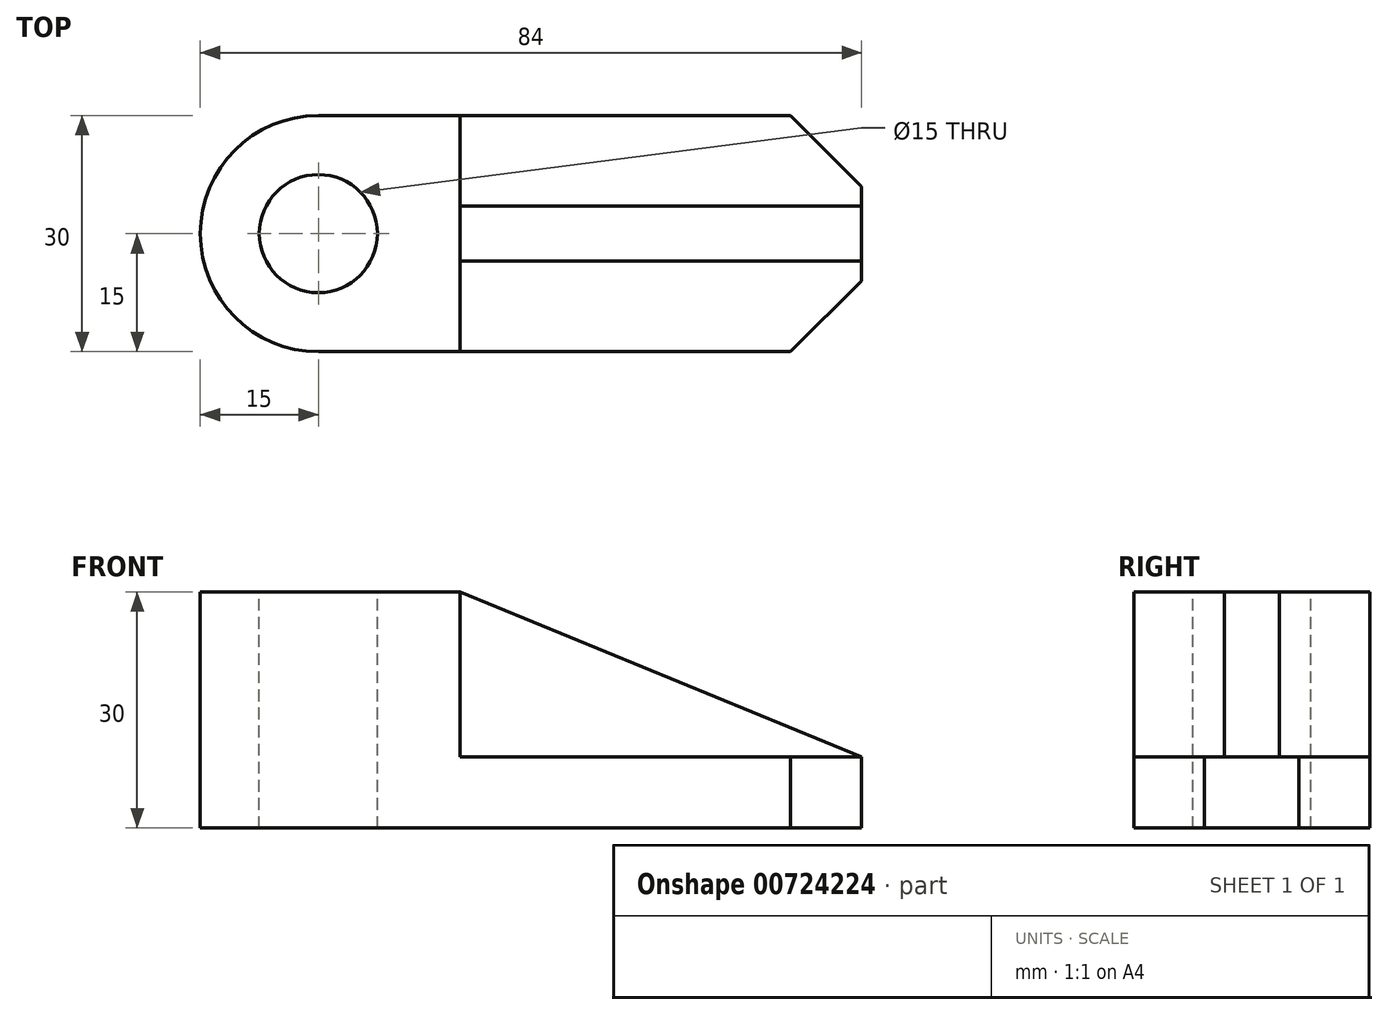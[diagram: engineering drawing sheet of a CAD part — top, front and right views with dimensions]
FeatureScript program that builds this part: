
annotation { "Feature Type Name" : "Feature", "Feature Type Description" : "" }
export const myFeature = defineFeature(function(context is Context, id is Id, definition is map)
    precondition{}
    {
        {
            var Q0;
            Q0=qCreatedBy(makeId("Top.planeOp"),FACE);
            var sketch = newSketch(context, id + "F0", { "sketchPlane" : qUnion([Q0])});
            skLineSegment(sketch, "E0", {"start": v(0, 0) * mm, "end": v(60, 0) * mm});
            skLineSegment(sketch, "E1", {"start": v(60, 0) * mm, "end": v(69, -9) * mm});
            skLineSegment(sketch, "E2", {"start": v(69, -9) * mm, "end": v(69, -21) * mm});
            skLineSegment(sketch, "E3", {"start": v(69, -21) * mm, "end": v(60, -30) * mm});
            skLineSegment(sketch, "E4", {"start": v(60, -30) * mm, "end": v(0, -30) * mm});
            skArc(sketch, "E5", {"start": v(0, 0) * mm, "mid": v(-15, -15) * mm, "end": v(0, -30) * mm});
            skSolve(sketch);
        }
        {
            var Q0;
            Q0 = qSketchRegion(id + "F0", true);
            extrude(context, id + "F1", {"entities" : qUnion([Q0]), "depth" : 9 * mm, "offsetDistance" : 25 * mm});
        }
        {
            var Q0;
            Q0=makeQuery(id+"F1.opExtrude","CAP_FACE",FACE,{"disambiguationData":[OSD([sQuery(id+"F0.wireOp",EDGE,"E0"),sQuery(id+"F0.wireOp",EDGE,"E1"),sQuery(id+"F0.wireOp",EDGE,"E2"),sQuery(id+"F0.wireOp",EDGE,"E3"),sQuery(id+"F0.wireOp",EDGE,"E4"),sQuery(id+"F0.wireOp",EDGE,"E5")])],"isStart":false});
            var sketch = newSketch(context, id + "F2", { "sketchPlane" : qUnion([Q0])});
            skLineSegment(sketch, "E6", {"start": v(18, 0) * mm, "end": v(18, -30) * mm});
            skSolve(sketch);
        }
        {
            var Q0;
            {var subQ0=sQuery(id+"F2.wireOp",EDGE,"E6");Q0=makeQuery(id+"F2.imprint","IMPRINT",FACE,{"disambiguationData":[TD([[makeQuery(id+"F2.imprint","IMPRINT",EDGE,{"derivedFrom":subQ0}),-1.0]])]});}
            extrude(context, id + "F3", {"entities" : qUnion([Q0]), "operationType" : NewBodyOperationType.ADD, "depth" : 21 * mm, "offsetDistance" : 25 * mm});
        }
        {
            var Q0;
            Q0=makeQuery(id+"F3.opExtrude","CAP_FACE",FACE,{"disambiguationData":[OSD([sQuery(id+"F0.wireOp",EDGE,"E0"),sQuery(id+"F0.wireOp",EDGE,"E4"),sQuery(id+"F0.wireOp",EDGE,"E5"),sQuery(id+"F2.wireOp",EDGE,"E6")])],"isStart":false});
            var sketch = newSketch(context, id + "F4", { "sketchPlane" : qUnion([Q0])});
            skCircle(sketch, "E7", {"center": v(0, -15) * mm, "radius": 7.5 * mm});
            skSolve(sketch);
        }
        {
            var Q0;
            Q0 = qSketchRegion(id + "F4", true);
            extrude(context, id + "F5", {"entities" : qUnion([Q0]), "operationType" : NewBodyOperationType.REMOVE, "oppositeDirection" : true, "depth" : 30 * mm, "offsetDistance" : 25 * mm});
        }
        {
            var Q0;
            Q0=makeQuery(id+"F1.opExtrude","CAP_FACE",FACE,{"disambiguationData":[OSD([sQuery(id+"F0.wireOp",EDGE,"E0"),sQuery(id+"F0.wireOp",EDGE,"E1"),sQuery(id+"F0.wireOp",EDGE,"E2"),sQuery(id+"F0.wireOp",EDGE,"E3"),sQuery(id+"F0.wireOp",EDGE,"E4"),sQuery(id+"F0.wireOp",EDGE,"E5")])],"isStart":false});
            var sketch = newSketch(context, id + "F6", { "sketchPlane" : qUnion([Q0])});
            skLineSegment(sketch, "E8", {"start": v(69, -11.5) * mm, "end": v(18, -11.5) * mm});
            skLineSegment(sketch, "E9", {"start": v(18, -11.5) * mm, "end": v(18, -18.5) * mm});
            skLineSegment(sketch, "E10", {"start": v(18, -18.5) * mm, "end": v(69, -18.5) * mm});
            skLineSegment(sketch, "E11", {"start": v(69, -18.5) * mm, "end": v(69, -11.5) * mm});
            skSolve(sketch);
        }
        {
            var Q0;
            Q0=makeQuery(id+"F6.imprint","IMPRINT",FACE,{"disambiguationData":[TD([[makeQuery(id+"F6.imprint","IMPRINT",EDGE,{"derivedFrom":sQuery(id+"F6.wireOp",EDGE,"E8")}),1.0]])]});
            extrude(context, id + "F7", {"entities" : qUnion([Q0]), "operationType" : NewBodyOperationType.ADD, "depth" : 21 * mm, "offsetDistance" : 25 * mm});
        }
        {
            var Q0;
            Q0=makeQuery(id+"F7.opExtrude","SWEPT_FACE",FACE,{"disambiguationData":[OSD([sQuery(id+"F6.wireOp",EDGE,"E10")])]});
            var sketch = newSketch(context, id + "F8", { "sketchPlane" : qUnion([Q0])});
            skLineSegment(sketch, "E12", {"start": v(18, 30) * mm, "end": v(69, 9) * mm});
            skLineSegment(sketch, "E13", {"start": v(69, 9) * mm, "end": v(69, 30) * mm});
            skLineSegment(sketch, "E14", {"start": v(69, 30) * mm, "end": v(18, 30) * mm});
            skSolve(sketch);
        }
        {
            var Q0;
            Q0 = qSketchRegion(id + "F8", true);
            extrude(context, id + "F9", {"entities" : qUnion([Q0]), "operationType" : NewBodyOperationType.REMOVE, "oppositeDirection" : true, "depth" : 25 * mm, "offsetDistance" : 25 * mm});
        }
    });
